# Revit family: highbay_11_midi_51hn11da4eda
name_source: partatom
category: Lighting Fixtures
units: mm (PartAtom-declared; Revit-internal decimal feet)

## family parameters
Cut with Voids When Loaded = No
Host = Face
Light Source = No
Part Type = Normal
Room Calculation Point = No
Round Connector Dimension = Use Diameter
Shared = No

## types (1)
- --- (1 x LED, 1490 lm, 8.2 W, 4000K)
    Apparent Load = 8 VA
    CIE Flux Codes = 85 97 100 100 100
    Color Rendering = 80
    Color Temperature = 4000K
    Default Elevation = 1800 mm
    Description = high bay luminaire Highbay 11 midi; direct symmetric narrow distribution, light control with lens of PMMA; UGR ≤ 19 (X = 4H | Y = 8H | S = 0.25H | reflection values 70/50/20); luminous flux: 10.000lm; light colour: 840, colour temperature: 4000K, MacAdam ≤ 2 SDCM (initial), colour rendering: CRI > 80; luminous efficacy: 209,6lm/W; rated service life: 100.000h (L95) at AT= 25°C; control: DALI 2; luminaire connection: terminal, 5-pole, max. 2.5mm² (cable entry for one cable, Ø 8.5..16mm); mains connection: 230..240V, AC/DC 0/50..60Hz; connected load: 47,7W; protection rating (complete): IP66; insulation class (complete): insulation class I (protective earthing); protection symbol: D; impact resistance: IK08; certification: CE, ENEC, VDE, UKCA; luminaire for central battery installations according to EN 60598-2-22, internal wiring halogen-free; luminaire Suitable for use in the food industry according to the specifications of IFS-Food, HACCP and/or BRC; LABS conformity tested according to VDMA 24364:2018-05; housing frame of high-performance plastic PA6, matt traffic white (RAL 9016); cover of PMMA; dimension (LxWxH): 474 x 442 x 72mm; permissible operating ambient temperature: -40..+70°C (reducing of maximum allowable ambient temperature of 5°C with ceiling mounting); packaging unit: 1 piece; (delivery without accessories; please order mounting accessories separately)
    Height = 72 mm
    Lamp = 1 x LED
    Lamp Light Flux = 1490 lm
    Lamp Power = 8.2 W
    Lamp count = 1
    Length = 474 mm
    Luminous efficacy = 182 lm/W
    Manufacturer = Siteco
    ModVariant = No
    Model = 51HN11DA4EDA
    Mounting Place = Ceiling
    Mounting Type = Pendant
    Number of Poles = 1
    OnlyDefault = Yes
    Power Factor = 1
    Product Name = Highbay 11 midi
    Product group = high bay luminaire
    ProductGroupID = 902
    Protection Class = Protection class I
    Protection Degree = IP 66
    RLX_Detail_Level = 1
    RLX_Emergency_Light_Flux = 0 lm
    RLX_Emergency_Type = 0
    RLX_Emergency_Type_DB = No
    RlxData = <blob elided: 76053 chars, md5=b4fa2c46>
    Socket = socket
    Standby Power = 0 W
    System Light Flux = 1490 lm
    System Power = 8 W
    Type Comments = : DC mode (central or group accumulator) initial emergency light level
    Type Image = l_1363240.jpg
    URL = http://relux.com
    VarID = @adj_022183
    Voltage = 0 V
    Weight = 0.00 kg
    Width = 442 mm

## geometry (parser evidence)
native form markers: Sweep x11
no freeform markers — native parametric forms only
